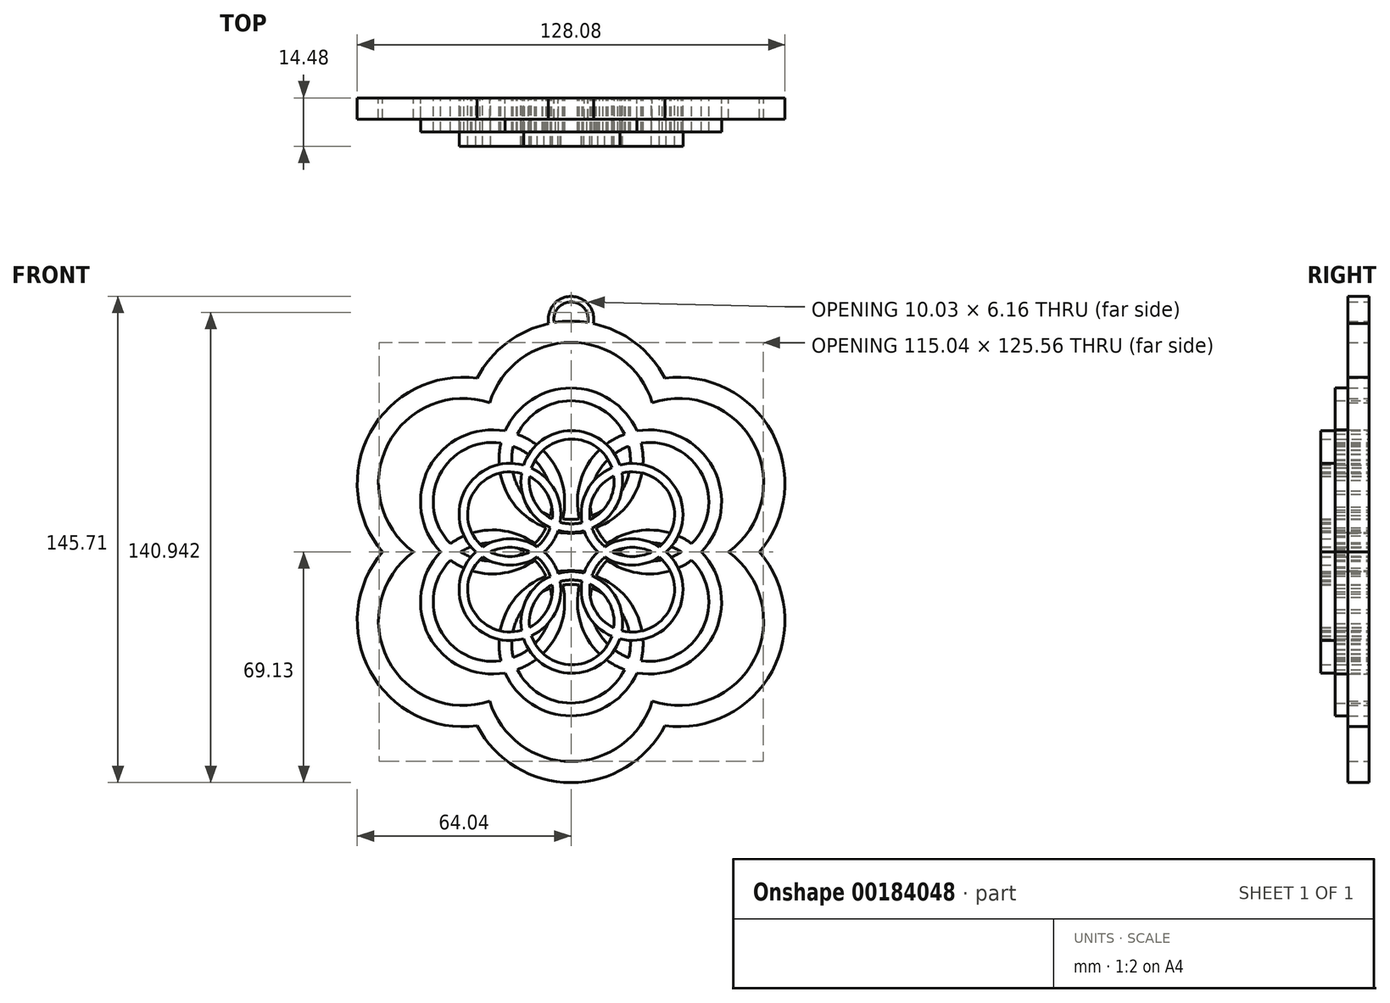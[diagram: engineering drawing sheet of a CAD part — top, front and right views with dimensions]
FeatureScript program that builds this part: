
annotation { "Feature Type Name" : "Feature", "Feature Type Description" : "" }
export const myFeature = defineFeature(function(context is Context, id is Id, definition is map)
    precondition{}
    {
        {
            var Q0;
            Q0=qCreatedBy(makeId("Front.planeOp"),FACE);
            var sketch = newSketch(context, id + "F0", { "sketchPlane" : qUnion([Q0])});
            skArc(sketch, "E0", {"start": v(-1.72, 12.04) * mm, "mid": v(-58.67, 38.27) * mm, "end": v(-12.73, -4.4) * mm});
            skArc(sketch, "E1", {"start": v(-7.98, 13.27) * mm, "mid": v(-52.97, 35.36) * mm, "end": v(-17.44, 0) * mm});
            skArc(sketch, "E2.MirrorC", {"start": v(8.14, 0) * mm, "mid": v(5.98, 2.84) * mm, "end": v(4.15, 5.9) * mm});
            skArc(sketch, "E3.MirrorC", {"start": v(12.73, 4.4) * mm, "mid": v(11.6, 5.88) * mm, "end": v(10.57, 7.44) * mm});
            skArc(sketch, "E4.MirrorC", {"start": v(7.98, -13.27) * mm, "mid": v(52.97, -35.36) * mm, "end": v(17.44, 0) * mm});
            skArc(sketch, "E5.MirrorC", {"start": v(1.72, -12.04) * mm, "mid": v(58.67, -38.27) * mm, "end": v(12.73, 4.4) * mm});
            skArc(sketch, "E6.MirrorC", {"start": v(-8.14, 0) * mm, "mid": v(-5.98, -2.84) * mm, "end": v(-4.15, -5.9) * mm});
            skArc(sketch, "E7.MirrorC", {"start": v(-12.73, -4.4) * mm, "mid": v(-11.6, -5.88) * mm, "end": v(-10.57, -7.44) * mm});
            skArc(sketch, "E8", {"start": v(-4.15, 5.9) * mm, "mid": v(0, 5.63) * mm, "end": v(4.15, 5.9) * mm});
            skArc(sketch, "E9", {"start": v(-1.72, 12.04) * mm, "mid": v(0, 11.98) * mm, "end": v(1.72, 12.04) * mm});
            skArc(sketch, "E10.MirrorC", {"start": v(7.98, -13.27) * mm, "mid": v(0, -62.78) * mm, "end": v(-7.98, -13.27) * mm});
            skArc(sketch, "E11.MirrorC", {"start": v(10.57, -7.44) * mm, "mid": v(0, -69.13) * mm, "end": v(-10.57, -7.44) * mm});
            skArc(sketch, "E12.trimOffspring", {"start": v(7.98, 13.27) * mm, "mid": v(52.97, 35.36) * mm, "end": v(17.44, 0) * mm});
            skArc(sketch, "E13.trimOffspring", {"start": v(1.72, 12.04) * mm, "mid": v(58.67, 38.27) * mm, "end": v(12.73, -4.4) * mm});
            skArc(sketch, "E14.trimOffspring", {"start": v(-1.72, -12.04) * mm, "mid": v(-58.67, -38.27) * mm, "end": v(-12.73, 4.4) * mm});
            skArc(sketch, "E15.trimOffspring", {"start": v(-7.98, -13.27) * mm, "mid": v(-52.97, -35.36) * mm, "end": v(-17.44, 0) * mm});
            skArc(sketch, "E16.trimOffspring", {"start": v(8.14, 0) * mm, "mid": v(5.98, -2.84) * mm, "end": v(4.15, -5.9) * mm});
            skArc(sketch, "E17.trimOffspring", {"start": v(12.73, -4.4) * mm, "mid": v(11.6, -5.88) * mm, "end": v(10.57, -7.44) * mm});
            skArc(sketch, "E18.trimOffspring", {"start": v(-8.14, 0) * mm, "mid": v(-5.98, 2.84) * mm, "end": v(-4.15, 5.9) * mm});
            skArc(sketch, "E19.trimOffspring", {"start": v(-4.15, -5.9) * mm, "mid": v(0, -5.63) * mm, "end": v(4.15, -5.9) * mm});
            skArc(sketch, "E20.trimOffspring", {"start": v(7.98, 13.27) * mm, "mid": v(0, 62.78) * mm, "end": v(-7.98, 13.27) * mm});
            skArc(sketch, "E21.trimOffspring", {"start": v(10.57, 7.44) * mm, "mid": v(0, 69.13) * mm, "end": v(-10.57, 7.44) * mm});
            skArc(sketch, "E22.trimOffspring", {"start": v(-12.73, 4.4) * mm, "mid": v(-11.6, 5.88) * mm, "end": v(-10.57, 7.44) * mm});
            skArc(sketch, "E23.trimOffspring", {"start": v(-1.72, -12.04) * mm, "mid": v(0, -11.98) * mm, "end": v(1.72, -12.04) * mm});
            skSolve(sketch);
        }
        {
            var Q0;
            Q0 = qSketchRegion(id + "F0", true);
            var Q1;
            Q1=makeQuery(id+"F0.imprint","IMPRINT",FACE,{"disambiguationData":[TD([[makeQuery(id+"F0.imprint","IMPRINT",EDGE,{"derivedFrom":sQuery(id+"F0.wireOp",EDGE,"E2.MirrorC")}),-1.0]])]});
            var Q2;
            Q2 = qSketchRegion(id + "F2", true);
            extrude(context, id + "F1", {"entities" : qUnion([Q0, Q1, Q2]), "depth" : 6.35 * mm});
        }
        {
            var Q0;
            Q0=qCreatedBy(makeId("Front.planeOp"),FACE);
            var sketch = newSketch(context, id + "F2", { "sketchPlane" : qUnion([Q0])});
            skArc(sketch, "E24", {"start": v(-19.74, 36.27) * mm, "mid": v(-42.57, 25.15) * mm, "end": v(-39.03, 0) * mm});
            skArc(sketch, "E25", {"start": v(-20.98, 32.6) * mm, "mid": v(-39.39, 23) * mm, "end": v(-36.14, 2.5) * mm});
            skArc(sketch, "E26.MirrorC", {"start": v(-33.04, 0) * mm, "mid": v(-23.5, 2.77) * mm, "end": v(-13.97, 0) * mm});
            skArc(sketch, "E27.MirrorC", {"start": v(-36.14, 2.5) * mm, "mid": v(-23.5, 6.58) * mm, "end": v(-10.87, 2.5) * mm});
            skArc(sketch, "E28.MirrorC", {"start": v(36.14, 2.5) * mm, "mid": v(23.5, 6.58) * mm, "end": v(10.87, 2.5) * mm});
            skArc(sketch, "E29.MirrorC", {"start": v(33.04, 0) * mm, "mid": v(23.5, 2.77) * mm, "end": v(13.97, 0) * mm});
            skArc(sketch, "E30.MirrorC", {"start": v(20.98, 32.6) * mm, "mid": v(39.39, 23) * mm, "end": v(36.14, 2.5) * mm});
            skArc(sketch, "E31.MirrorC", {"start": v(19.74, 36.27) * mm, "mid": v(42.57, 25.15) * mm, "end": v(39.03, 0) * mm});
            skArc(sketch, "E32", {"start": v(-20.98, 32.6) * mm, "mid": v(-19.06, 17.38) * mm, "end": v(-7.5, 7.28) * mm});
            skArc(sketch, "E33", {"start": v(-17.3, 31.67) * mm, "mid": v(-15.7, 19.17) * mm, "end": v(-6.22, 10.87) * mm});
            skArc(sketch, "E34.MirrorC", {"start": v(7.5, -7.28) * mm, "mid": v(19.06, -17.38) * mm, "end": v(20.98, -32.6) * mm});
            skArc(sketch, "E35.MirrorC", {"start": v(6.22, -10.87) * mm, "mid": v(15.7, -19.17) * mm, "end": v(17.3, -31.67) * mm});
            skArc(sketch, "E36.trimOffspring", {"start": v(-2.52, 9.93) * mm, "mid": v(0, 9.75) * mm, "end": v(2.52, 9.93) * mm});
            skArc(sketch, "E37.trimOffspring", {"start": v(-2.52, 9.93) * mm, "mid": v(-4.45, 25.16) * mm, "end": v(-16.01, 35.26) * mm});
            skArc(sketch, "E38.trimOffspring", {"start": v(-6.22, 10.87) * mm, "mid": v(-7.81, 23.37) * mm, "end": v(-17.3, 31.67) * mm});
            skArc(sketch, "E39.trimOffspring", {"start": v(-3.77, 6.27) * mm, "mid": v(0, 5.94) * mm, "end": v(3.77, 6.27) * mm});
            skArc(sketch, "E40.trimOffspring", {"start": v(-33.04, 0) * mm, "mid": v(-23.5, -2.77) * mm, "end": v(-13.97, 0) * mm});
            skArc(sketch, "E41.trimOffspring", {"start": v(-36.14, -2.5) * mm, "mid": v(-23.5, -6.58) * mm, "end": v(-10.87, -2.5) * mm});
            skArc(sketch, "E42.trimOffspring", {"start": v(-10.87, -2.5) * mm, "mid": v(-8.99, -4.75) * mm, "end": v(-7.5, -7.28) * mm});
            skArc(sketch, "E43.trimOffspring", {"start": v(-7.99, 0) * mm, "mid": v(-5.6, -2.95) * mm, "end": v(-3.77, -6.27) * mm});
            skArc(sketch, "E44.trimOffspring", {"start": v(-7.99, 0) * mm, "mid": v(-5.6, 2.95) * mm, "end": v(-3.77, 6.27) * mm});
            skArc(sketch, "E45.trimOffspring", {"start": v(-10.87, 2.5) * mm, "mid": v(-8.99, 4.75) * mm, "end": v(-7.5, 7.28) * mm});
            skArc(sketch, "E46.trimOffspring", {"start": v(16.01, 35.26) * mm, "mid": v(0, 45.3) * mm, "end": v(-16.01, 35.26) * mm});
            skArc(sketch, "E47.trimOffspring", {"start": v(19.74, 36.27) * mm, "mid": v(0, 49.12) * mm, "end": v(-19.74, 36.27) * mm});
            skArc(sketch, "E48.trimOffspring", {"start": v(33.04, 0) * mm, "mid": v(23.5, -2.77) * mm, "end": v(13.97, 0) * mm});
            skArc(sketch, "E49.trimOffspring", {"start": v(36.14, -2.5) * mm, "mid": v(23.5, -6.58) * mm, "end": v(10.87, -2.5) * mm});
            skArc(sketch, "E50.trimOffspring", {"start": v(10.87, 2.5) * mm, "mid": v(8.99, 4.75) * mm, "end": v(7.5, 7.28) * mm});
            skArc(sketch, "E51.trimOffspring", {"start": v(7.99, 0) * mm, "mid": v(5.6, 2.95) * mm, "end": v(3.77, 6.27) * mm});
            skArc(sketch, "E52.trimOffspring", {"start": v(7.99, 0) * mm, "mid": v(5.6, -2.95) * mm, "end": v(3.77, -6.27) * mm});
            skArc(sketch, "E53.trimOffspring", {"start": v(10.87, -2.5) * mm, "mid": v(8.99, -4.75) * mm, "end": v(7.5, -7.28) * mm});
            skArc(sketch, "E54.trimOffspring", {"start": v(6.22, -10.87) * mm, "mid": v(7.81, -23.37) * mm, "end": v(17.3, -31.67) * mm});
            skArc(sketch, "E55.trimOffspring", {"start": v(2.52, -9.93) * mm, "mid": v(4.45, -25.16) * mm, "end": v(16.01, -35.26) * mm});
            skArc(sketch, "E56.trimOffspring", {"start": v(19.74, -36.27) * mm, "mid": v(0, -49.12) * mm, "end": v(-19.74, -36.27) * mm});
            skArc(sketch, "E57.trimOffspring", {"start": v(20.98, -32.6) * mm, "mid": v(39.39, -23) * mm, "end": v(36.14, -2.5) * mm});
            skArc(sketch, "E58.trimOffspring", {"start": v(16.01, -35.26) * mm, "mid": v(0, -45.3) * mm, "end": v(-16.01, -35.26) * mm});
            skArc(sketch, "E59.trimOffspring", {"start": v(19.74, -36.27) * mm, "mid": v(42.57, -25.15) * mm, "end": v(39.03, 0) * mm});
            skArc(sketch, "E60.trimOffspring", {"start": v(-17.3, -31.67) * mm, "mid": v(-15.7, -19.17) * mm, "end": v(-6.22, -10.87) * mm});
            skArc(sketch, "E61.trimOffspring", {"start": v(-20.98, -32.6) * mm, "mid": v(-39.39, -23) * mm, "end": v(-36.14, -2.5) * mm});
            skArc(sketch, "E62.trimOffspring", {"start": v(-20.98, -32.6) * mm, "mid": v(-19.06, -17.38) * mm, "end": v(-7.5, -7.28) * mm});
            skArc(sketch, "E63.trimOffspring", {"start": v(-19.74, -36.27) * mm, "mid": v(-42.57, -25.15) * mm, "end": v(-39.03, 0) * mm});
            skArc(sketch, "E64.trimOffspring", {"start": v(-2.52, -9.93) * mm, "mid": v(0, -9.75) * mm, "end": v(2.52, -9.93) * mm});
            skArc(sketch, "E65.trimOffspring", {"start": v(-3.77, -6.27) * mm, "mid": v(0, -5.94) * mm, "end": v(3.77, -6.27) * mm});
            skArc(sketch, "E66.trimOffspring", {"start": v(-6.22, -10.87) * mm, "mid": v(-7.81, -23.37) * mm, "end": v(-17.3, -31.67) * mm});
            skArc(sketch, "E67.trimOffspring", {"start": v(-2.52, -9.93) * mm, "mid": v(-4.45, -25.16) * mm, "end": v(-16.01, -35.26) * mm});
            skArc(sketch, "E68.trimOffspring", {"start": v(2.52, 9.93) * mm, "mid": v(4.45, 25.16) * mm, "end": v(16.01, 35.26) * mm});
            skArc(sketch, "E69.trimOffspring", {"start": v(6.22, 10.87) * mm, "mid": v(15.7, 19.17) * mm, "end": v(17.3, 31.67) * mm});
            skArc(sketch, "E70.trimOffspring", {"start": v(7.5, 7.28) * mm, "mid": v(19.06, 17.38) * mm, "end": v(20.98, 32.6) * mm});
            skArc(sketch, "E71.trimOffspring", {"start": v(6.22, 10.87) * mm, "mid": v(7.81, 23.37) * mm, "end": v(17.3, 31.67) * mm});
            skSolve(sketch);
        }
        {
            var Q0;
            Q0=makeQuery(id+"F2.imprint","IMPRINT",FACE,{"disambiguationData":[TD([[makeQuery(id+"F2.imprint","IMPRINT",EDGE,{"derivedFrom":sQuery(id+"F2.wireOp",EDGE,"E24")}),1.0]])]});
            extrude(context, id + "F3", {"entities" : qUnion([Q0]), "operationType" : NewBodyOperationType.ADD, "depth" : 5.08 * mm});
        }
        {
            var Q0;
            Q0=qCreatedBy(makeId("Front.planeOp"),FACE);
            var sketch = newSketch(context, id + "F4", { "sketchPlane" : qUnion([Q0])});
            skArc(sketch, "E72", {"start": v(-14.23, 25.99) * mm, "mid": v(-31.65, 18.64) * mm, "end": v(-28.52, 0) * mm});
            skArc(sketch, "E73", {"start": v(-14.84, 23.52) * mm, "mid": v(-29.52, 17.24) * mm, "end": v(-26.45, 1.57) * mm});
            skArc(sketch, "E74", {"start": v(-14.84, 23.52) * mm, "mid": v(-13.26, 13.97) * mm, "end": v(-6.24, 7.3) * mm});
            skArc(sketch, "E75", {"start": v(-12.41, 22.56) * mm, "mid": v(-11.01, 15.16) * mm, "end": v(-5.67, 9.85) * mm});
            skArc(sketch, "E76.MirrorC", {"start": v(-12.41, -22.56) * mm, "mid": v(-11.01, -15.16) * mm, "end": v(-5.67, -9.85) * mm});
            skArc(sketch, "E77.MirrorC", {"start": v(-14.84, -23.52) * mm, "mid": v(-13.26, -13.97) * mm, "end": v(-6.24, -7.3) * mm});
            skArc(sketch, "E78.MirrorC", {"start": v(24.09, 0) * mm, "mid": v(18.3, -1.4) * mm, "end": v(12.5, 0) * mm});
            skArc(sketch, "E79.MirrorC", {"start": v(26.45, -1.57) * mm, "mid": v(18.3, -3.94) * mm, "end": v(10.13, -1.57) * mm});
            skArc(sketch, "E80.MirrorC", {"start": v(5.7, -9.66) * mm, "mid": v(7.13, -17.36) * mm, "end": v(12.8, -22.75) * mm});
            skArc(sketch, "E81.MirrorC", {"start": v(3.26, -8.78) * mm, "mid": v(4.9, -18.57) * mm, "end": v(12.2, -25.27) * mm});
            skArc(sketch, "E82.MirrorC", {"start": v(-24.09, 0) * mm, "mid": v(-18.3, 1.4) * mm, "end": v(-12.5, 0) * mm});
            skArc(sketch, "E83.MirrorC", {"start": v(-26.45, 1.57) * mm, "mid": v(-18.3, 3.94) * mm, "end": v(-10.13, 1.57) * mm});
            skArc(sketch, "E84.trimOffspring", {"start": v(-3.85, 6.42) * mm, "mid": v(0.01, 5.87) * mm, "end": v(3.89, 6.32) * mm});
            skArc(sketch, "E85.trimOffspring", {"start": v(-3.24, 8.89) * mm, "mid": v(0, 8.41) * mm, "end": v(3.26, 8.78) * mm});
            skArc(sketch, "E86.trimOffspring", {"start": v(-5.67, 9.85) * mm, "mid": v(-7.07, 17.25) * mm, "end": v(-12.41, 22.56) * mm});
            skArc(sketch, "E87.trimOffspring", {"start": v(-3.24, 8.89) * mm, "mid": v(-4.83, 18.44) * mm, "end": v(-11.85, 25.11) * mm});
            skArc(sketch, "E88.trimOffspring", {"start": v(-26.45, -1.57) * mm, "mid": v(-18.3, -3.94) * mm, "end": v(-10.13, -1.57) * mm});
            skArc(sketch, "E89.trimOffspring", {"start": v(-24.09, 0) * mm, "mid": v(-18.3, -1.4) * mm, "end": v(-12.5, 0) * mm});
            skArc(sketch, "E90.trimOffspring", {"start": v(-14.84, -23.52) * mm, "mid": v(-29.52, -17.24) * mm, "end": v(-26.45, -1.57) * mm});
            skArc(sketch, "E91.trimOffspring", {"start": v(-14.23, -25.99) * mm, "mid": v(-31.65, -18.64) * mm, "end": v(-28.52, 0) * mm});
            skArc(sketch, "E92.trimOffspring", {"start": v(-3.85, -6.42) * mm, "mid": v(0.01, -5.87) * mm, "end": v(3.89, -6.32) * mm});
            skArc(sketch, "E93.trimOffspring", {"start": v(-5.67, -9.85) * mm, "mid": v(-7.07, -17.25) * mm, "end": v(-12.41, -22.56) * mm});
            skArc(sketch, "E94.trimOffspring", {"start": v(-3.24, -8.89) * mm, "mid": v(0, -8.41) * mm, "end": v(3.26, -8.78) * mm});
            skArc(sketch, "E95.trimOffspring", {"start": v(-3.24, -8.89) * mm, "mid": v(-4.83, -18.44) * mm, "end": v(-11.85, -25.11) * mm});
            skArc(sketch, "E96.trimOffspring", {"start": v(5.7, -9.66) * mm, "mid": v(11.37, -15.05) * mm, "end": v(12.8, -22.75) * mm});
            skArc(sketch, "E97.trimOffspring", {"start": v(6.3, -7.14) * mm, "mid": v(13.6, -13.84) * mm, "end": v(15.24, -23.63) * mm});
            skArc(sketch, "E98.trimOffspring", {"start": v(15.24, -23.63) * mm, "mid": v(29.61, -17.06) * mm, "end": v(26.45, -1.57) * mm});
            skArc(sketch, "E99.trimOffspring", {"start": v(12.2, -25.27) * mm, "mid": v(0.12, -33.8) * mm, "end": v(-11.85, -25.11) * mm});
            skArc(sketch, "E100.trimOffspring", {"start": v(14.6, -26.09) * mm, "mid": v(31.74, -18.47) * mm, "end": v(28.52, 0) * mm});
            skArc(sketch, "E101.trimOffspring", {"start": v(14.6, -26.09) * mm, "mid": v(0.15, -36.35) * mm, "end": v(-14.23, -25.99) * mm});
            skArc(sketch, "E102.trimOffspring", {"start": v(26.45, 1.57) * mm, "mid": v(18.3, 3.94) * mm, "end": v(10.13, 1.57) * mm});
            skArc(sketch, "E103.trimOffspring", {"start": v(24.09, 0) * mm, "mid": v(18.3, 1.4) * mm, "end": v(12.5, 0) * mm});
            skArc(sketch, "E104.trimOffspring", {"start": v(8.07, 0) * mm, "mid": v(5.58, -2.9) * mm, "end": v(3.89, -6.32) * mm});
            skArc(sketch, "E105.trimOffspring", {"start": v(8.07, 0) * mm, "mid": v(5.58, 2.9) * mm, "end": v(3.89, 6.32) * mm});
            skArc(sketch, "E106.trimOffspring", {"start": v(10.13, 1.57) * mm, "mid": v(7.83, 4.1) * mm, "end": v(6.3, 7.14) * mm});
            skArc(sketch, "E107.trimOffspring", {"start": v(10.13, -1.57) * mm, "mid": v(7.83, -4.1) * mm, "end": v(6.3, -7.14) * mm});
            skArc(sketch, "E108.trimOffspring", {"start": v(6.3, 7.14) * mm, "mid": v(13.6, 13.84) * mm, "end": v(15.24, 23.63) * mm});
            skArc(sketch, "E109.trimOffspring", {"start": v(5.7, 9.66) * mm, "mid": v(11.37, 15.05) * mm, "end": v(12.8, 22.75) * mm});
            skArc(sketch, "E110.trimOffspring", {"start": v(5.7, 9.66) * mm, "mid": v(7.13, 17.36) * mm, "end": v(12.8, 22.75) * mm});
            skArc(sketch, "E111.trimOffspring", {"start": v(3.26, 8.78) * mm, "mid": v(4.9, 18.57) * mm, "end": v(12.2, 25.27) * mm});
            skArc(sketch, "E112.trimOffspring", {"start": v(12.2, 25.27) * mm, "mid": v(0.12, 33.8) * mm, "end": v(-11.85, 25.11) * mm});
            skArc(sketch, "E113.trimOffspring", {"start": v(14.6, 26.09) * mm, "mid": v(31.74, 18.47) * mm, "end": v(28.52, 0) * mm});
            skArc(sketch, "E114.trimOffspring", {"start": v(14.6, 26.09) * mm, "mid": v(0.15, 36.35) * mm, "end": v(-14.23, 25.99) * mm});
            skArc(sketch, "E115.trimOffspring", {"start": v(15.24, 23.63) * mm, "mid": v(29.61, 17.06) * mm, "end": v(26.45, 1.57) * mm});
            skArc(sketch, "E116.trimOffspring", {"start": v(-8.07, 0) * mm, "mid": v(-5.55, -2.94) * mm, "end": v(-3.85, -6.42) * mm});
            skArc(sketch, "E117.trimOffspring", {"start": v(-10.13, 1.57) * mm, "mid": v(-7.79, 4.16) * mm, "end": v(-6.24, 7.3) * mm});
            skArc(sketch, "E118.trimOffspring", {"start": v(-10.13, -1.57) * mm, "mid": v(-7.79, -4.16) * mm, "end": v(-6.24, -7.3) * mm});
            skArc(sketch, "E119.trimOffspring", {"start": v(-8.07, 0) * mm, "mid": v(-5.55, 2.94) * mm, "end": v(-3.85, 6.42) * mm});
            skSolve(sketch);
        }
        {
            var Q0;
            Q0 = qSketchRegion(id + "F4", true);
            extrude(context, id + "F5", {"entities" : qUnion([Q0]), "depth" : 3.8 * mm});
        }
        {
            var Q0;
            Q0=qCreatedBy(makeId("Front.planeOp"),FACE);
            var sketch = newSketch(context, id + "F6", { "sketchPlane" : qUnion([Q0])});
            skCircle(sketch, "E120", {"center": v(0, 69.77) * mm, "radius": 6.81 * mm});
            skCircle(sketch, "E121", {"center": v(0, 69.77) * mm, "radius": 5.12 * mm});
            skSolve(sketch);
        }
        {
            var Q0;
            Q0=makeQuery(id+"F6.imprint","IMPRINT",FACE,{"disambiguationData":[TD([[makeQuery(id+"F6.imprint","IMPRINT",EDGE,{"derivedFrom":sQuery(id+"F6.wireOp",EDGE,"E120")}),1.0]])]});
            extrude(context, id + "F7", {"entities" : qUnion([Q0]), "operationType" : NewBodyOperationType.ADD, "depth" : 6.35 * mm});
        }
        {
            var Q0;
            Q0 = qSketchRegion(id + "F2", true);
            extrude(context, id + "F8", {"entities" : qUnion([Q0]), "operationType" : NewBodyOperationType.ADD, "depth" : 10.16 * mm});
        }
        {
            var Q0;
            Q0 = qSketchRegion(id + "F4", true);
            extrude(context, id + "F9", {"entities" : qUnion([Q0]), "operationType" : NewBodyOperationType.ADD, "depth" : 14.48 * mm});
        }
    });
